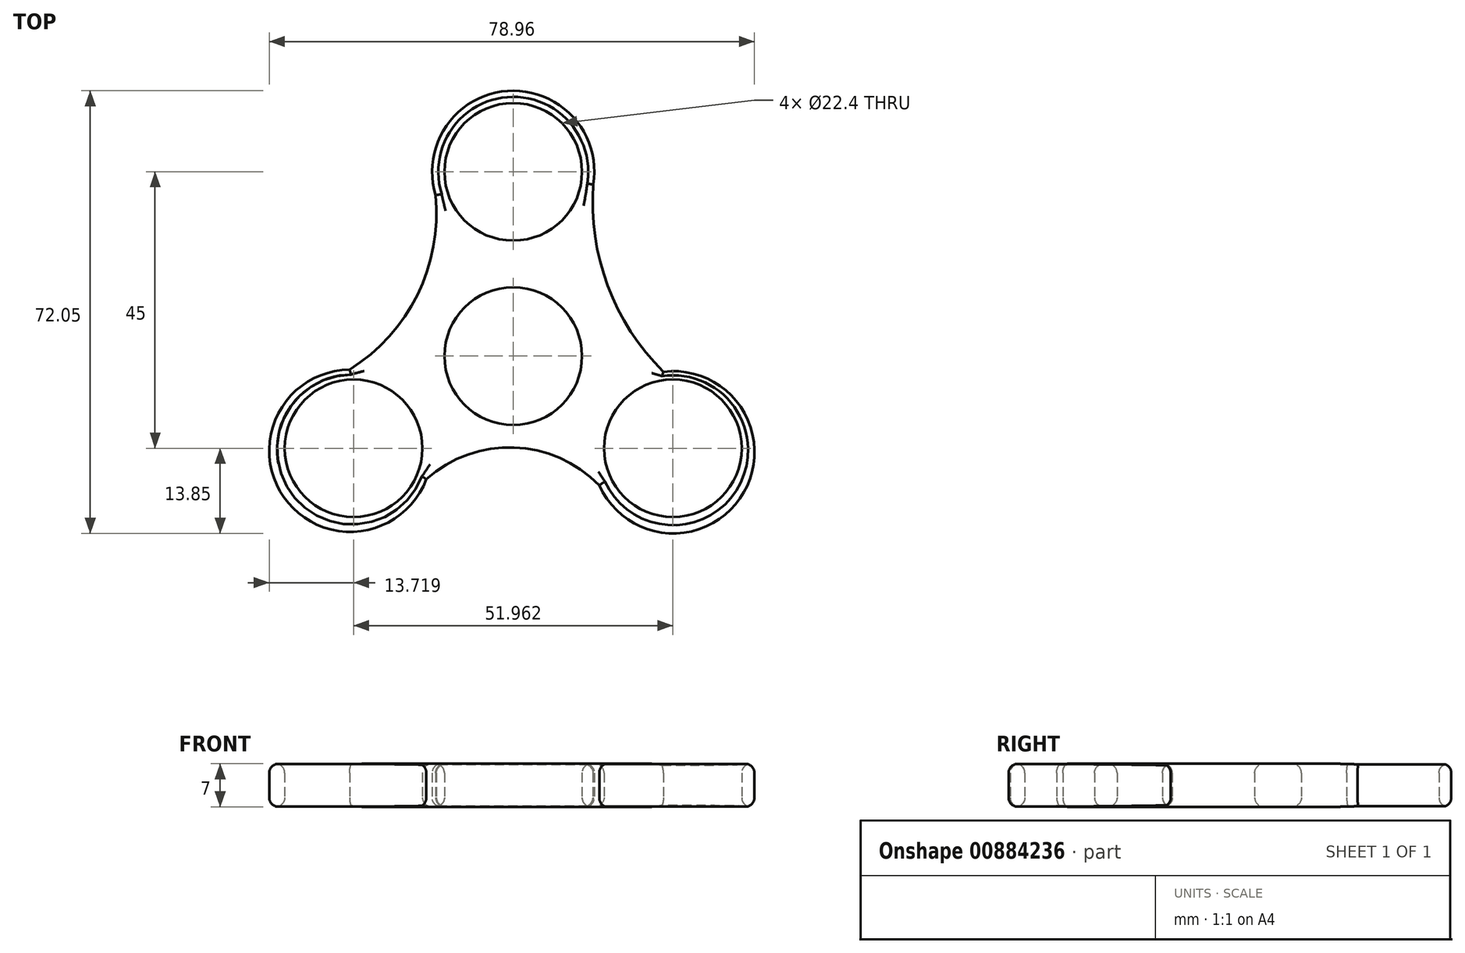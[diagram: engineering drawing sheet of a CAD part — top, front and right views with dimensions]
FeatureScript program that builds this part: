
annotation { "Feature Type Name" : "Feature", "Feature Type Description" : "" }
export const myFeature = defineFeature(function(context is Context, id is Id, definition is map)
    precondition{}
    {
        {
            var Q0;
            Q0=qCreatedBy(makeId("Top.planeOp"),FACE);
            var sketch = newSketch(context, id + "F0", { "sketchPlane" : qUnion([Q0])});
            skCircle(sketch, "E0", {"center": v(0, 0) * mm, "radius": 11.2 * mm});
            skCircle(sketch, "E1", {"center": v(0, 30) * mm, "radius": 11.2 * mm});
            skArc(sketch, "E2", {"start": v(13.04, 27.95) * mm, "mid": v(-0.9, 43.17) * mm, "end": v(-12.63, 26.18) * mm});
            skArc(sketch, "E3.1.0", {"start": v(-26.63, -2.2) * mm, "mid": v(-37.32, -22.96) * mm, "end": v(-14.15, -20.03) * mm});
            skArc(sketch, "E3.2.0", {"start": v(14, -21.02) * mm, "mid": v(37.55, -22.15) * mm, "end": v(24.45, -2.55) * mm});
            skPoint(sketch, "E3.center", {"position": v(-0.15, -0.35) * mm});
            skPoint(sketch, "E4.endSnap0", {"position": v(13.03, 7.17) * mm});
            skArc(sketch, "E5", {"start": v(-26.63, -2.2) * mm, "mid": v(-15.58, 10) * mm, "end": v(-12.63, 26.18) * mm});
            skArc(sketch, "E6", {"start": v(14, -21.02) * mm, "mid": v(0.13, -14.88) * mm, "end": v(-14.15, -20.03) * mm});
            skCircle(sketch, "E7.1.0", {"center": v(-25.98, -15) * mm, "radius": 11.2 * mm});
            skCircle(sketch, "E7.2.0", {"center": v(25.98, -15) * mm, "radius": 11.2 * mm});
            skArc(sketch, "E8.trimOffspring", {"start": v(13.04, 27.95) * mm, "mid": v(15.38, 11.44) * mm, "end": v(24.45, -2.55) * mm});
            skPoint(sketch, "E9.trimOffspring.end.orphan", {"position": v(11.08, 7.17) * mm});
            skSolve(sketch);
        }
        {
            var Q0;
            Q0=makeQuery(id+"F0.imprint","IMPRINT",FACE,{"disambiguationData":[TD([[makeQuery(id+"F0.imprint","IMPRINT",EDGE,{"derivedFrom":sQuery(id+"F0.wireOp",EDGE,"E0")}),-1.0]])]});
            extrude(context, id + "F1", {"entities" : qUnion([Q0]), "depth" : 7 * mm, "offsetDistance" : 25 * mm});
        }
        {
            var Q0;
            Q0=makeQuery(id+"F1.opExtrude","CAP_FACE",FACE,{"disambiguationData":[OSD([sQuery(id+"F0.wireOp",EDGE,"E0"),sQuery(id+"F0.wireOp",EDGE,"E1"),sQuery(id+"F0.wireOp",EDGE,"E2"),sQuery(id+"F0.wireOp",EDGE,"E3.1.0"),sQuery(id+"F0.wireOp",EDGE,"E3.2.0"),sQuery(id+"F0.wireOp",EDGE,"E5"),sQuery(id+"F0.wireOp",EDGE,"E6"),sQuery(id+"F0.wireOp",EDGE,"E7.1.0"),sQuery(id+"F0.wireOp",EDGE,"E7.2.0"),sQuery(id+"F0.wireOp",EDGE,"E8.trimOffspring")])],"isStart":true});
            var Q1;
            Q1=makeQuery(id+"F1.opExtrude","CAP_FACE",FACE,{"disambiguationData":[OSD([sQuery(id+"F0.wireOp",EDGE,"E0"),sQuery(id+"F0.wireOp",EDGE,"E1"),sQuery(id+"F0.wireOp",EDGE,"E2"),sQuery(id+"F0.wireOp",EDGE,"E3.1.0"),sQuery(id+"F0.wireOp",EDGE,"E3.2.0"),sQuery(id+"F0.wireOp",EDGE,"E5"),sQuery(id+"F0.wireOp",EDGE,"E6"),sQuery(id+"F0.wireOp",EDGE,"E7.1.0"),sQuery(id+"F0.wireOp",EDGE,"E7.2.0"),sQuery(id+"F0.wireOp",EDGE,"E8.trimOffspring")])],"isStart":false});
            fillet(context, id + "F2", {"entities" : qUnion([Q0, Q1]), "radius" : 1.5 * mm, "tangentPropagation" : true, "allowEdgeOverflow" : false});
        }
    });
